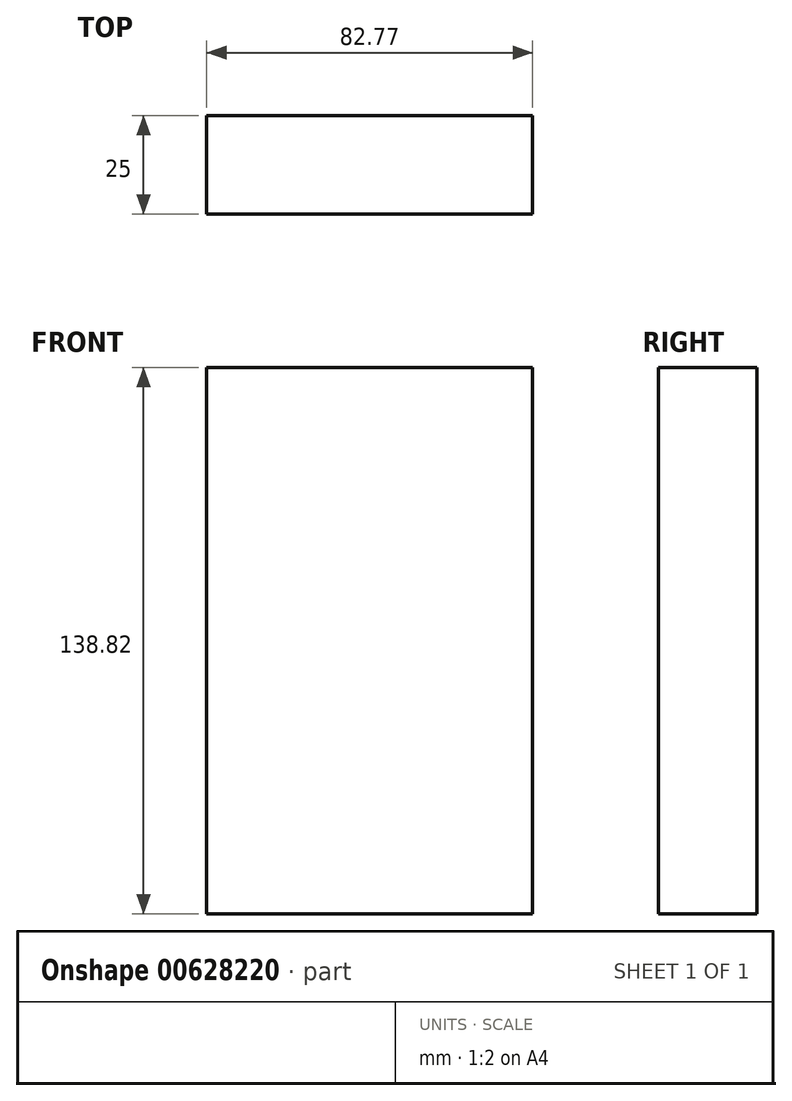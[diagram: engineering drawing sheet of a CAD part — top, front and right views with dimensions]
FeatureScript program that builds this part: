
annotation { "Feature Type Name" : "Feature", "Feature Type Description" : "" }
export const myFeature = defineFeature(function(context is Context, id is Id, definition is map)
    precondition{}
    {
        {
            var Q0;
            Q0=qCreatedBy(makeId("Front.planeOp"),FACE);
            var sketch = newSketch(context, id + "F0", { "sketchPlane" : qUnion([Q0])});
            skLineSegment(sketch, "E0.bottom", {"start": v(-42.68, 61.94) * mm, "end": v(40.1, 61.94) * mm});
            skLineSegment(sketch, "E0.top", {"start": v(-42.68, -76.88) * mm, "end": v(40.1, -76.88) * mm});
            skLineSegment(sketch, "E0.left", {"start": v(-42.68, 61.94) * mm, "end": v(-42.68, -76.88) * mm});
            skLineSegment(sketch, "E0.right", {"start": v(40.1, 61.94) * mm, "end": v(40.1, -76.88) * mm});
            skSolve(sketch);
        }
        {
            var Q0;
            Q0=makeQuery(id+"F0.imprint","IMPRINT",FACE,{"disambiguationData":[TD([[makeQuery(id+"F0.imprint","IMPRINT",EDGE,{"derivedFrom":sQuery(id+"F0.wireOp",EDGE,"E0.bottom")}),-1.0]])]});
            extrude(context, id + "F1", {"entities" : qUnion([Q0]), "depth" : 25 * mm, "offsetDistance" : 25 * mm});
        }
    });
